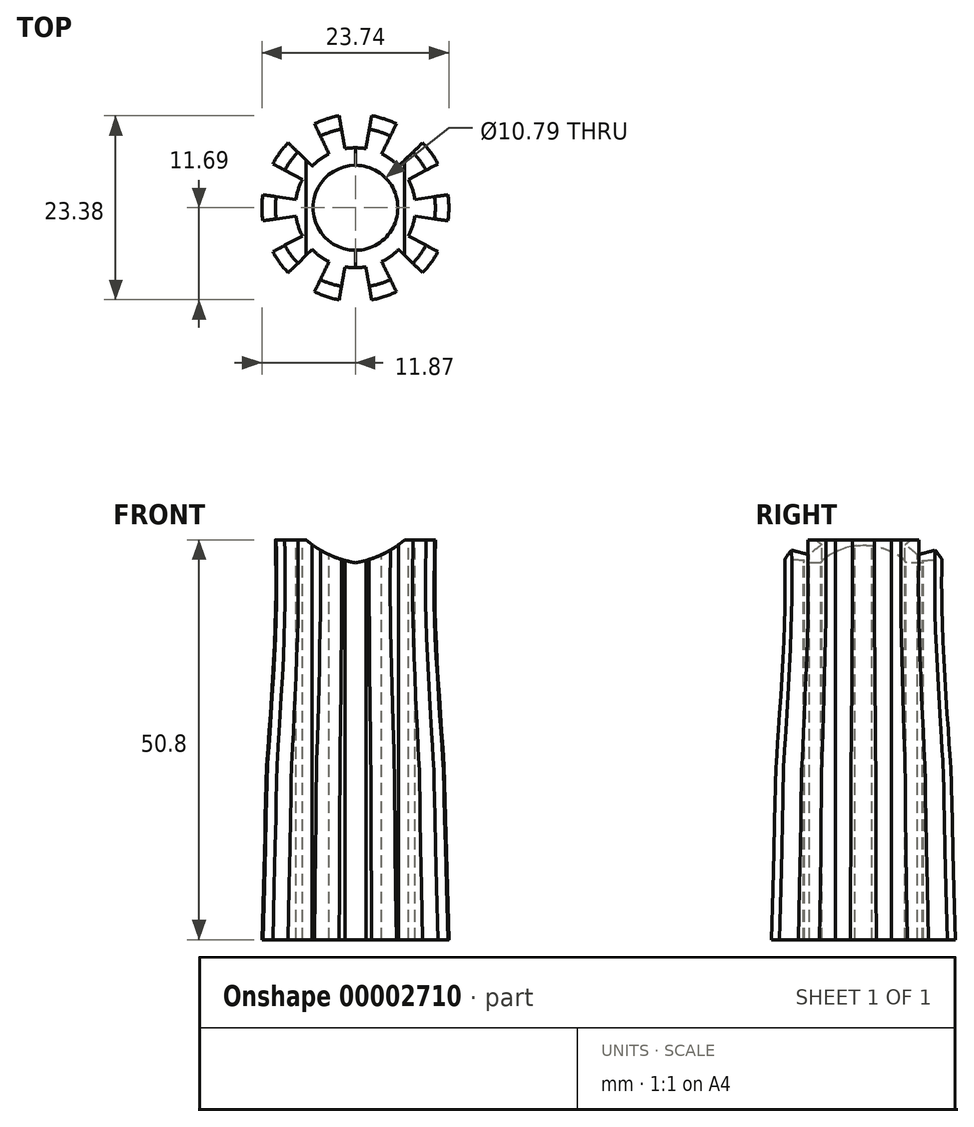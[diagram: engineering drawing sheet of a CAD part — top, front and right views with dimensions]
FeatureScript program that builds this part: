
annotation { "Feature Type Name" : "Feature", "Feature Type Description" : "" }
export const myFeature = defineFeature(function(context is Context, id is Id, definition is map)
    precondition{}
    {
        {
            var Q0;
            Q0=qCreatedBy(makeId("Front.planeOp"),FACE);
            var sketch = newSketch(context, id + "F0", { "sketchPlane" : qUnion([Q0])});
            skFitSpline(sketch, "E0", {"points": [v(11.87, 0) * mm, v(11.18, 23.33) * mm, v(10.16, 40.6) * mm, v(10.16, 50.8) * mm], "startDerivative": vector(-5.28, 176.5) * mm, "endDerivative": vector(0.28, 37.42) * mm});
            skLineSegment(sketch, "E1", {"start": v(10.16, 50.8) * mm, "end": v(0, 50.8) * mm});
            skLineSegment(sketch, "E2", {"start": v(0, 50.8) * mm, "end": v(0, 0) * mm});
            skLineSegment(sketch, "E3", {"start": v(0, 0) * mm, "end": v(11.87, 0) * mm});
            skSolve(sketch);
        }
        {
            var Q0;
            Q0=makeQuery(id+"F0.imprint","IMPRINT",FACE,{"disambiguationData":[TD([[makeQuery(id+"F0.imprint","IMPRINT",EDGE,{"derivedFrom":sQuery(id+"F0.wireOp",EDGE,"E0")}),1.0]])]});
            var Q1;
            Q1=sQuery(id+"F0.wireOp",EDGE,"E2");
            revolve(context, id + "F1", {"entities" : qUnion([Q0]), "axis" : qUnion([Q1]), "revolveType" : RevolveType.FULL});
        }
        {
            var Q0;
            Q0=makeQuery(id+"F1.opRevolve","SWEPT_FACE",FACE,{"disambiguationData":[OSD([sQuery(id+"F0.wireOp",EDGE,"E1")])]});
            var sketch = newSketch(context, id + "F2", { "sketchPlane" : qUnion([Q0])});
            skCircle(sketch, "E4", {"center": v(0, 0) * mm, "radius": 5.4 * mm});
            skSolve(sketch);
        }
        {
            var Q0;
            Q0=makeQuery(id+"F2.imprint","IMPRINT",FACE,{"disambiguationData":[TD([[makeQuery(id+"F2.imprint","IMPRINT",EDGE,{"derivedFrom":sQuery(id+"F2.wireOp",EDGE,"E4")}),1.0]])]});
            extrude(context, id + "F3", {"entities" : qUnion([Q0]), "operationType" : NewBodyOperationType.REMOVE, "endBound" : BoundingType.THROUGH_ALL, "oppositeDirection" : true, "depth" : 25.4 * mm});
        }
        {
            var Q0;
            Q0=makeQuery(id+"F1.opRevolve","SWEPT_FACE",FACE,{"disambiguationData":[OSD([sQuery(id+"F0.wireOp",EDGE,"E1")])]});
            var sketch = newSketch(context, id + "F4", { "sketchPlane" : qUnion([Q0])});
            skCircle(sketch, "E5.0", {"center": v(0, 0) * mm, "radius": 11.87 * mm});
            skLineSegment(sketch, "E6", {"start": v(0, 0) * mm, "end": v(0, 11.87) * mm, "construction": true});
            skCircle(sketch, "E7", {"center": v(0, 0) * mm, "radius": 7.62 * mm});
            skLineSegment(sketch, "E8", {"start": v(0, 0) * mm, "end": v(2.23, 12.64) * mm});
            skLineSegment(sketch, "E9", {"start": v(0, 0) * mm, "end": v(0, -11.87) * mm, "construction": true});
            skLineSegment(sketch, "E10", {"start": v(0, 0) * mm, "end": v(-6.98, 9.6) * mm, "construction": true});
            skLineSegment(sketch, "E11", {"start": v(0, 0) * mm, "end": v(-11.3, 3.67) * mm, "construction": true});
            skLineSegment(sketch, "E12", {"start": v(0, 0) * mm, "end": v(-11.3, -3.67) * mm, "construction": true});
            skLineSegment(sketch, "E13", {"start": v(0, 0) * mm, "end": v(-5.91, 12.12) * mm});
            skLineSegment(sketch, "E14", {"start": v(0, 0) * mm, "end": v(-12.6, 6.7) * mm});
            skLineSegment(sketch, "E15", {"start": v(-12.6, 6.7) * mm, "end": v(-11.3, 3.67) * mm});
            skLineSegment(sketch, "E16", {"start": v(2.23, 12.64) * mm, "end": v(0, 11.87) * mm});
            skLineSegment(sketch, "E17", {"start": v(-5.91, 12.12) * mm, "end": v(-6.98, 9.6) * mm});
            skLineSegment(sketch, "E18", {"start": v(0, 0) * mm, "end": v(-13.09, -1.84) * mm});
            skLineSegment(sketch, "E19", {"start": v(-13.09, -1.84) * mm, "end": v(-11.3, -3.67) * mm});
            skLineSegment(sketch, "E20.0.MirrorCS", {"start": v(0, 0) * mm, "end": v(-2.23, 12.64) * mm});
            skLineSegment(sketch, "E21.0.MirrorCS", {"start": v(-2.23, 12.64) * mm, "end": v(0, 11.87) * mm});
            skLineSegment(sketch, "E22.0.MirrorCS", {"start": v(0, 0) * mm, "end": v(-9.7, 9.37) * mm});
            skLineSegment(sketch, "E23.0.MirrorCS", {"start": v(-9.7, 9.37) * mm, "end": v(-6.98, 9.6) * mm});
            skLineSegment(sketch, "E24.0.MirrorCS", {"start": v(0, 0) * mm, "end": v(-14.14, 1.99) * mm});
            skLineSegment(sketch, "E25.0.MirrorCS", {"start": v(-14.14, 1.99) * mm, "end": v(-11.3, 3.67) * mm});
            skLineSegment(sketch, "E26.0.MirrorCS", {"start": v(0, 0) * mm, "end": v(-11.67, -6.2) * mm});
            skLineSegment(sketch, "E27.0.MirrorCS", {"start": v(-11.67, -6.2) * mm, "end": v(-11.3, -3.67) * mm});
            skLineSegment(sketch, "E28", {"start": v(0, 0) * mm, "end": v(-6.98, -9.6) * mm, "construction": true});
            skLineSegment(sketch, "E29", {"start": v(0, 0) * mm, "end": v(0, -11.87) * mm});
            skLineSegment(sketch, "E30", {"start": v(0, 0) * mm, "end": v(6.98, -9.6) * mm, "construction": true});
            skLineSegment(sketch, "E31", {"start": v(0, 0) * mm, "end": v(11.3, -3.67) * mm, "construction": true});
            skLineSegment(sketch, "E32", {"start": v(0, 0) * mm, "end": v(11.3, 3.67) * mm, "construction": true});
            skLineSegment(sketch, "E33", {"start": v(0, 0) * mm, "end": v(6.98, 9.6) * mm, "construction": true});
            skLineSegment(sketch, "E34", {"start": v(0, 0) * mm, "end": v(-10.06, -9.72) * mm});
            skLineSegment(sketch, "E35", {"start": v(-10.06, -9.72) * mm, "end": v(-6.98, -9.6) * mm});
            skLineSegment(sketch, "E36", {"start": v(0, 0) * mm, "end": v(-2.29, -12.96) * mm});
            skLineSegment(sketch, "E37", {"start": v(-2.29, -12.96) * mm, "end": v(0, -11.87) * mm});
            skLineSegment(sketch, "E38", {"start": v(0, 0) * mm, "end": v(12.03, -6.4) * mm});
            skLineSegment(sketch, "E39", {"start": v(12.03, -6.4) * mm, "end": v(11.3, -3.67) * mm});
            skLineSegment(sketch, "E40", {"start": v(0, 0) * mm, "end": v(13.55, 1.9) * mm});
            skLineSegment(sketch, "E41", {"start": v(13.55, 1.9) * mm, "end": v(11.3, 3.67) * mm});
            skLineSegment(sketch, "E42", {"start": v(0, 0) * mm, "end": v(9.6, 9.26) * mm});
            skLineSegment(sketch, "E43", {"start": v(9.6, 9.26) * mm, "end": v(6.98, 9.6) * mm});
            skLineSegment(sketch, "E44", {"start": v(0, 0) * mm, "end": v(5.81, -11.92) * mm});
            skLineSegment(sketch, "E45", {"start": v(5.81, -11.92) * mm, "end": v(6.98, -9.6) * mm});
            skLineSegment(sketch, "E46.0.MirrorCS", {"start": v(5.84, 11.98) * mm, "end": v(6.98, 9.6) * mm});
            skLineSegment(sketch, "E47.0.MirrorCS", {"start": v(0, 0) * mm, "end": v(5.84, 11.98) * mm});
            skLineSegment(sketch, "E48.0.MirrorCS", {"start": v(0, 0) * mm, "end": v(12.08, 6.42) * mm});
            skLineSegment(sketch, "E49.0.MirrorCS", {"start": v(12.08, 6.42) * mm, "end": v(11.3, 3.67) * mm});
            skLineSegment(sketch, "E50.0.MirrorCS", {"start": v(0, 0) * mm, "end": v(13.49, -1.9) * mm});
            skLineSegment(sketch, "E51.0.MirrorCS", {"start": v(13.49, -1.9) * mm, "end": v(11.3, -3.67) * mm});
            skLineSegment(sketch, "E52.0.MirrorCS", {"start": v(0, 0) * mm, "end": v(9.54, -9.21) * mm});
            skLineSegment(sketch, "E53.0.MirrorCS", {"start": v(9.54, -9.21) * mm, "end": v(6.98, -9.6) * mm});
            skLineSegment(sketch, "E54.0.MirrorCS", {"start": v(0, 0) * mm, "end": v(2.29, -12.96) * mm});
            skLineSegment(sketch, "E55.0.MirrorCS", {"start": v(2.29, -12.96) * mm, "end": v(0, -11.87) * mm});
            skLineSegment(sketch, "E56.0.MirrorCS", {"start": v(0, 0) * mm, "end": v(-6.13, -12.57) * mm});
            skLineSegment(sketch, "E57.0.MirrorCS", {"start": v(-6.13, -12.57) * mm, "end": v(-6.98, -9.6) * mm});
            skSolve(sketch);
        }
        {
            var Q0;
            {var subQ3=sQuery(id+"F4.wireOp",EDGE,"E8");var subQ5=sQuery(id+"F4.wireOp",EDGE,"E5.0");var subQ6=makeQuery(id+"F4.imprint","INTERSECT",VERTEX,{"derivedFrom":[subQ5,subQ3]});Q0=makeQuery(id+"F4.imprint","IMPRINT",FACE,{"disambiguationData":[TD([[makeQuery(id+"F4.imprint","IMPRINT",EDGE,{"disambiguationData":[TD([[subQ6,-1.0]])],"derivedFrom":subQ5}),1.0]])]});}
            var Q1;
            {var subQ3=sQuery(id+"F4.wireOp",EDGE,"E8");var subQ5=sQuery(id+"F4.wireOp",EDGE,"E7");var subQ6=makeQuery(id+"F4.imprint","INTERSECT",VERTEX,{"derivedFrom":[subQ5,subQ3]});Q1=makeQuery(id+"F4.imprint","IMPRINT",FACE,{"disambiguationData":[TD([[makeQuery(id+"F4.imprint","IMPRINT",EDGE,{"disambiguationData":[TD([[subQ6,-1.0]])],"derivedFrom":subQ5}),-1.0]])]});}
            var Q2;
            {var subQ3=sQuery(id+"F4.wireOp",EDGE,"E42");var subQ5=sQuery(id+"F4.wireOp",EDGE,"E5.0");var subQ7=makeQuery(id+"F4.imprint","INTERSECT",VERTEX,{"derivedFrom":[subQ5,subQ3]});Q2=makeQuery(id+"F4.imprint","IMPRINT",FACE,{"disambiguationData":[TD([[makeQuery(id+"F4.imprint","IMPRINT",EDGE,{"disambiguationData":[TD([[subQ7,-1.0]])],"derivedFrom":subQ5}),1.0]])]});}
            var Q3;
            {var subQ3=sQuery(id+"F4.wireOp",EDGE,"E42");var subQ5=sQuery(id+"F4.wireOp",EDGE,"E7");var subQ6=makeQuery(id+"F4.imprint","INTERSECT",VERTEX,{"derivedFrom":[subQ5,subQ3]});Q3=makeQuery(id+"F4.imprint","IMPRINT",FACE,{"disambiguationData":[TD([[makeQuery(id+"F4.imprint","IMPRINT",EDGE,{"disambiguationData":[TD([[subQ6,-1.0]])],"derivedFrom":subQ5}),-1.0]])]});}
            var Q4;
            {var subQ3=sQuery(id+"F4.wireOp",EDGE,"E40");var subQ5=sQuery(id+"F4.wireOp",EDGE,"E5.0");var subQ6=makeQuery(id+"F4.imprint","INTERSECT",VERTEX,{"derivedFrom":[subQ5,subQ3]});Q4=makeQuery(id+"F4.imprint","IMPRINT",FACE,{"disambiguationData":[TD([[makeQuery(id+"F4.imprint","IMPRINT",EDGE,{"disambiguationData":[TD([[subQ6,-1.0]])],"derivedFrom":subQ5}),1.0]])]});}
            var Q5;
            {var subQ1=sQuery(id+"F4.wireOp",EDGE,"E48.0.MirrorCS");var subQ5=sQuery(id+"F4.wireOp",EDGE,"E7");var subQ6=makeQuery(id+"F4.imprint","INTERSECT",VERTEX,{"derivedFrom":[subQ5,subQ1]});Q5=makeQuery(id+"F4.imprint","IMPRINT",FACE,{"disambiguationData":[TD([[makeQuery(id+"F4.imprint","IMPRINT",EDGE,{"disambiguationData":[TD([[subQ6,1.0]])],"derivedFrom":subQ5}),-1.0]])]});}
            var Q6;
            {var subQ3=sQuery(id+"F4.wireOp",EDGE,"E38");var subQ5=sQuery(id+"F4.wireOp",EDGE,"E5.0");var subQ7=makeQuery(id+"F4.imprint","INTERSECT",VERTEX,{"derivedFrom":[subQ5,subQ3]});Q6=makeQuery(id+"F4.imprint","IMPRINT",FACE,{"disambiguationData":[TD([[makeQuery(id+"F4.imprint","IMPRINT",EDGE,{"disambiguationData":[TD([[subQ7,-1.0]])],"derivedFrom":subQ5}),1.0]])]});}
            var Q7;
            {var subQ3=sQuery(id+"F4.wireOp",EDGE,"E38");var subQ5=sQuery(id+"F4.wireOp",EDGE,"E7");var subQ7=makeQuery(id+"F4.imprint","INTERSECT",VERTEX,{"derivedFrom":[subQ5,subQ3]});Q7=makeQuery(id+"F4.imprint","IMPRINT",FACE,{"disambiguationData":[TD([[makeQuery(id+"F4.imprint","IMPRINT",EDGE,{"disambiguationData":[TD([[subQ7,-1.0]])],"derivedFrom":subQ5}),-1.0]])]});}
            var Q8;
            {var subQ3=sQuery(id+"F4.wireOp",EDGE,"E44");var subQ5=sQuery(id+"F4.wireOp",EDGE,"E5.0");var subQ7=makeQuery(id+"F4.imprint","INTERSECT",VERTEX,{"derivedFrom":[subQ5,subQ3]});Q8=makeQuery(id+"F4.imprint","IMPRINT",FACE,{"disambiguationData":[TD([[makeQuery(id+"F4.imprint","IMPRINT",EDGE,{"disambiguationData":[TD([[subQ7,-1.0]])],"derivedFrom":subQ5}),1.0]])]});}
            var Q9;
            {var subQ3=sQuery(id+"F4.wireOp",EDGE,"E44");var subQ5=sQuery(id+"F4.wireOp",EDGE,"E7");var subQ7=makeQuery(id+"F4.imprint","INTERSECT",VERTEX,{"derivedFrom":[subQ5,subQ3]});Q9=makeQuery(id+"F4.imprint","IMPRINT",FACE,{"disambiguationData":[TD([[makeQuery(id+"F4.imprint","IMPRINT",EDGE,{"disambiguationData":[TD([[subQ7,-1.0]])],"derivedFrom":subQ5}),-1.0]])]});}
            var Q10;
            {var subQ3=sQuery(id+"F4.wireOp",EDGE,"E29");var subQ5=sQuery(id+"F4.wireOp",EDGE,"E7");var subQ7=makeQuery(id+"F4.imprint","INTERSECT",VERTEX,{"derivedFrom":[subQ5,subQ3]});Q10=makeQuery(id+"F4.imprint","IMPRINT",FACE,{"disambiguationData":[TD([[makeQuery(id+"F4.imprint","IMPRINT",EDGE,{"disambiguationData":[TD([[subQ7,-1.0]])],"derivedFrom":subQ5}),-1.0]])]});}
            var Q11;
            {var subQ1=sQuery(id+"F4.wireOp",EDGE,"E54.0.MirrorCS");var subQ5=sQuery(id+"F4.wireOp",EDGE,"E5.0");var subQ6=makeQuery(id+"F4.imprint","INTERSECT",VERTEX,{"derivedFrom":[subQ5,subQ1]});Q11=makeQuery(id+"F4.imprint","IMPRINT",FACE,{"disambiguationData":[TD([[makeQuery(id+"F4.imprint","IMPRINT",EDGE,{"disambiguationData":[TD([[subQ6,1.0]])],"derivedFrom":subQ1}),-1.0]])]});}
            var Q12;
            {var subQ1=sQuery(id+"F4.wireOp",EDGE,"E36");var subQ5=sQuery(id+"F4.wireOp",EDGE,"E5.0");var subQ6=makeQuery(id+"F4.imprint","INTERSECT",VERTEX,{"derivedFrom":[subQ5,subQ1]});Q12=makeQuery(id+"F4.imprint","IMPRINT",FACE,{"disambiguationData":[TD([[makeQuery(id+"F4.imprint","IMPRINT",EDGE,{"disambiguationData":[TD([[subQ6,1.0]])],"derivedFrom":subQ1}),1.0]])]});}
            var Q13;
            {var subQ1=sQuery(id+"F4.wireOp",EDGE,"E36");var subQ5=sQuery(id+"F4.wireOp",EDGE,"E7");var subQ6=makeQuery(id+"F4.imprint","INTERSECT",VERTEX,{"derivedFrom":[subQ5,subQ1]});Q13=makeQuery(id+"F4.imprint","IMPRINT",FACE,{"disambiguationData":[TD([[makeQuery(id+"F4.imprint","IMPRINT",EDGE,{"disambiguationData":[TD([[subQ6,-1.0]])],"derivedFrom":subQ5}),-1.0]])]});}
            var Q14;
            {var subQ3=sQuery(id+"F4.wireOp",EDGE,"E34");var subQ5=sQuery(id+"F4.wireOp",EDGE,"E7");var subQ7=makeQuery(id+"F4.imprint","INTERSECT",VERTEX,{"derivedFrom":[subQ5,subQ3]});Q14=makeQuery(id+"F4.imprint","IMPRINT",FACE,{"disambiguationData":[TD([[makeQuery(id+"F4.imprint","IMPRINT",EDGE,{"disambiguationData":[TD([[subQ7,-1.0]])],"derivedFrom":subQ5}),-1.0]])]});}
            var Q15;
            {var subQ3=sQuery(id+"F4.wireOp",EDGE,"E5.0");var subQ5=sQuery(id+"F4.wireOp",EDGE,"E34");var subQ7=makeQuery(id+"F4.imprint","INTERSECT",VERTEX,{"derivedFrom":[subQ3,subQ5]});Q15=makeQuery(id+"F4.imprint","IMPRINT",FACE,{"disambiguationData":[TD([[makeQuery(id+"F4.imprint","IMPRINT",EDGE,{"disambiguationData":[TD([[subQ7,-1.0]])],"derivedFrom":subQ3}),1.0]])]});}
            var Q16;
            {var subQ3=sQuery(id+"F4.wireOp",EDGE,"E18");var subQ5=sQuery(id+"F4.wireOp",EDGE,"E7");var subQ7=makeQuery(id+"F4.imprint","INTERSECT",VERTEX,{"derivedFrom":[subQ5,subQ3]});Q16=makeQuery(id+"F4.imprint","IMPRINT",FACE,{"disambiguationData":[TD([[makeQuery(id+"F4.imprint","IMPRINT",EDGE,{"disambiguationData":[TD([[subQ7,-1.0]])],"derivedFrom":subQ5}),-1.0]])]});}
            var Q17;
            {var subQ3=sQuery(id+"F4.wireOp",EDGE,"E18");var subQ5=sQuery(id+"F4.wireOp",EDGE,"E5.0");var subQ6=makeQuery(id+"F4.imprint","INTERSECT",VERTEX,{"derivedFrom":[subQ5,subQ3]});Q17=makeQuery(id+"F4.imprint","IMPRINT",FACE,{"disambiguationData":[TD([[makeQuery(id+"F4.imprint","IMPRINT",EDGE,{"disambiguationData":[TD([[subQ6,-1.0]])],"derivedFrom":subQ5}),1.0]])]});}
            var Q18;
            {var subQ3=sQuery(id+"F4.wireOp",EDGE,"E14");var subQ5=sQuery(id+"F4.wireOp",EDGE,"E7");var subQ7=makeQuery(id+"F4.imprint","INTERSECT",VERTEX,{"derivedFrom":[subQ5,subQ3]});Q18=makeQuery(id+"F4.imprint","IMPRINT",FACE,{"disambiguationData":[TD([[makeQuery(id+"F4.imprint","IMPRINT",EDGE,{"disambiguationData":[TD([[subQ7,-1.0]])],"derivedFrom":subQ5}),-1.0]])]});}
            var Q19;
            {var subQ3=sQuery(id+"F4.wireOp",EDGE,"E14");var subQ5=sQuery(id+"F4.wireOp",EDGE,"E5.0");var subQ7=makeQuery(id+"F4.imprint","INTERSECT",VERTEX,{"derivedFrom":[subQ5,subQ3]});Q19=makeQuery(id+"F4.imprint","IMPRINT",FACE,{"disambiguationData":[TD([[makeQuery(id+"F4.imprint","IMPRINT",EDGE,{"disambiguationData":[TD([[subQ7,-1.0]])],"derivedFrom":subQ5}),1.0]])]});}
            var Q20;
            {var subQ3=sQuery(id+"F4.wireOp",EDGE,"E5.0");var subQ5=sQuery(id+"F4.wireOp",EDGE,"E13");var subQ7=makeQuery(id+"F4.imprint","INTERSECT",VERTEX,{"derivedFrom":[subQ3,subQ5]});Q20=makeQuery(id+"F4.imprint","IMPRINT",FACE,{"disambiguationData":[TD([[makeQuery(id+"F4.imprint","IMPRINT",EDGE,{"disambiguationData":[TD([[subQ7,-1.0]])],"derivedFrom":subQ3}),1.0]])]});}
            var Q21;
            {var subQ3=sQuery(id+"F4.wireOp",EDGE,"E13");var subQ5=sQuery(id+"F4.wireOp",EDGE,"E7");var subQ7=makeQuery(id+"F4.imprint","INTERSECT",VERTEX,{"derivedFrom":[subQ5,subQ3]});Q21=makeQuery(id+"F4.imprint","IMPRINT",FACE,{"disambiguationData":[TD([[makeQuery(id+"F4.imprint","IMPRINT",EDGE,{"disambiguationData":[TD([[subQ7,-1.0]])],"derivedFrom":subQ5}),-1.0]])]});}
            extrude(context, id + "F5", {"entities" : qUnion([Q0, Q1, Q2, Q3, Q4, Q5, Q6, Q7, Q8, Q9, Q10, Q11, Q12, Q13, Q14, Q15, Q16, Q17, Q18, Q19, Q20, Q21]), "operationType" : NewBodyOperationType.REMOVE, "endBound" : BoundingType.THROUGH_ALL, "oppositeDirection" : true, "depth" : 25.4 * mm});
        }
        {
            var Q0;
            Q0=qCreatedBy(makeId("Front.planeOp"),FACE);
            var sketch = newSketch(context, id + "F6", { "sketchPlane" : qUnion([Q0])});
            skPoint(sketch, "E58.0", {"position": v(10.06, 50.8) * mm});
            skPoint(sketch, "E59.0", {"position": v(-10.06, 50.8) * mm});
            skLineSegment(sketch, "E60", {"start": v(-10.06, 50.8) * mm, "end": v(-6.25, 50.8) * mm});
            skArc(sketch, "E61", {"start": v(-6.25, 50.8) * mm, "mid": v(-3.33, 48.91) * mm, "end": v(0, 47.9) * mm});
            skLineSegment(sketch, "E62", {"start": v(0, 47.9) * mm, "end": v(0, 50.77) * mm, "construction": true});
            skArc(sketch, "E63.0.MirrorCS", {"start": v(6.25, 50.8) * mm, "mid": v(3.33, 48.91) * mm, "end": v(0, 47.9) * mm});
            skLineSegment(sketch, "E64", {"start": v(-6.25, 50.8) * mm, "end": v(6.25, 50.8) * mm});
            skSolve(sketch);
        }
        {
            var Q0;
            Q0=makeQuery(id+"F6.imprint","IMPRINT",FACE,{"disambiguationData":[TD([[makeQuery(id+"F6.imprint","IMPRINT",EDGE,{"derivedFrom":sQuery(id+"F6.wireOp",EDGE,"E61")}),1.0]])]});
            extrude(context, id + "F7", {"entities" : qUnion([Q0]), "operationType" : NewBodyOperationType.REMOVE, "endBound" : BoundingType.SYMMETRIC, "oppositeDirection" : true, "depth" : 25.4 * mm});
        }
    });
